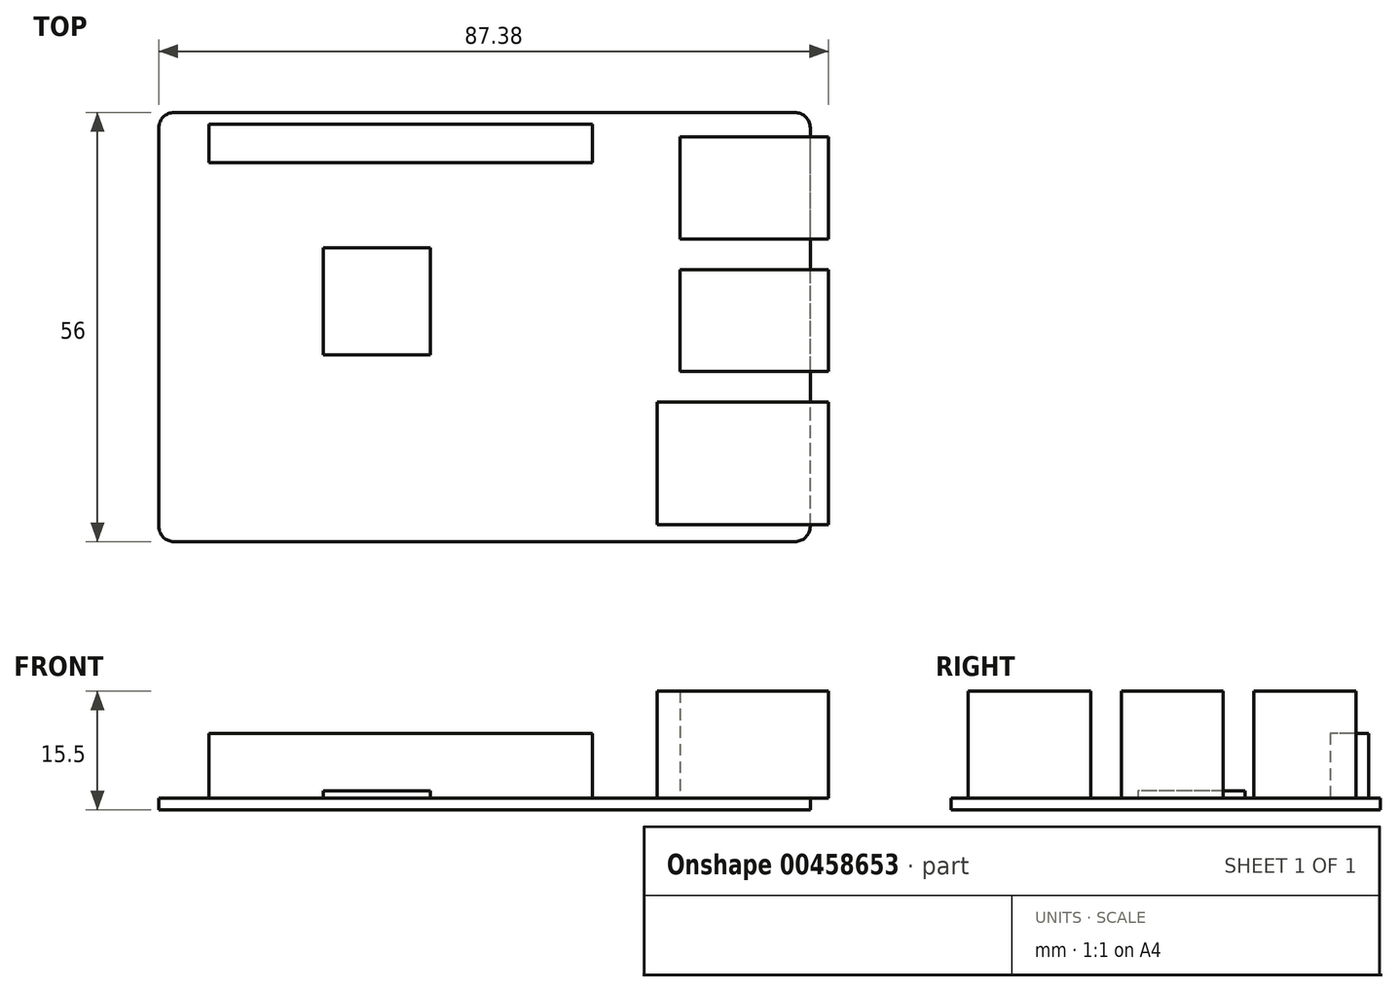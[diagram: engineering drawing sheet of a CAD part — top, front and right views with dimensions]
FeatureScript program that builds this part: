
annotation { "Feature Type Name" : "Feature", "Feature Type Description" : "" }
export const myFeature = defineFeature(function(context is Context, id is Id, definition is map)
    precondition{}
    {
        {
            var Q0;
            Q0=qCreatedBy(makeId("Top.planeOp"),FACE);
            var sketch = newSketch(context, id + "F0", { "sketchPlane" : qUnion([Q0])});
            skLineSegment(sketch, "E0.bottom", {"start": v(42.5, -28) * mm, "end": v(-42.5, -28) * mm});
            skLineSegment(sketch, "E0.top", {"start": v(42.5, 28) * mm, "end": v(-42.5, 28) * mm});
            skLineSegment(sketch, "E0.left", {"start": v(42.5, -28) * mm, "end": v(42.5, 28) * mm});
            skLineSegment(sketch, "E0.right", {"start": v(-42.5, -28) * mm, "end": v(-42.5, 28) * mm});
            skPoint(sketch, "E0.middle", {"position": v(0, 0) * mm});
            skSolve(sketch);
        }
        {
            var Q0;
            Q0=makeQuery(id+"F0.imprint","IMPRINT",FACE,{"disambiguationData":[TD([[makeQuery(id+"F0.imprint","IMPRINT",EDGE,{"derivedFrom":sQuery(id+"F0.wireOp",EDGE,"E0.bottom")}),-1.0]])]});
            extrude(context, id + "F1", {"entities" : qUnion([Q0]), "depth" : 1.5 * mm});
        }
        {
            var Q0;
            Q0=makeQuery(id+"F1.opExtrude","SWEPT_EDGE",EDGE,{"disambiguationData":[OSD([sQuery(id+"F0.wireOp",EDGE,"E0.bottom"),sQuery(id+"F0.wireOp",EDGE,"E0.right")])]});
            var Q1;
            Q1=makeQuery(id+"F1.opExtrude","SWEPT_EDGE",EDGE,{"disambiguationData":[OSD([sQuery(id+"F0.wireOp",EDGE,"E0.top"),sQuery(id+"F0.wireOp",EDGE,"E0.right")])]});
            var Q2;
            Q2=makeQuery(id+"F1.opExtrude","SWEPT_EDGE",EDGE,{"disambiguationData":[OSD([sQuery(id+"F0.wireOp",EDGE,"E0.bottom"),sQuery(id+"F0.wireOp",EDGE,"E0.left")])]});
            var Q3;
            Q3=makeQuery(id+"F1.opExtrude","SWEPT_EDGE",EDGE,{"disambiguationData":[OSD([sQuery(id+"F0.wireOp",EDGE,"E0.top"),sQuery(id+"F0.wireOp",EDGE,"E0.left")])]});
            fillet(context, id + "F2", {"entities" : qUnion([Q0, Q1, Q2, Q3]), "radius" : 2 * mm, "tangentPropagation" : true, "allowEdgeOverflow" : false});
        }
        {
            var Q0;
            Q0=makeQuery(id+"F1.opExtrude","CAP_FACE",FACE,{"disambiguationData":[OSD([sQuery(id+"F0.wireOp",EDGE,"E0.bottom"),sQuery(id+"F0.wireOp",EDGE,"E0.top"),sQuery(id+"F0.wireOp",EDGE,"E0.left"),sQuery(id+"F0.wireOp",EDGE,"E0.right")])],"isStart":false});
            var sketch = newSketch(context, id + "F3", { "sketchPlane" : qUnion([Q0])});
            skLineSegment(sketch, "E1.bottom", {"start": v(-35.96, 26.48) * mm, "end": v(14.04, 26.48) * mm});
            skLineSegment(sketch, "E1.top", {"start": v(-35.96, 21.48) * mm, "end": v(14.04, 21.48) * mm});
            skLineSegment(sketch, "E1.left", {"start": v(-35.96, 26.48) * mm, "end": v(-35.96, 21.48) * mm});
            skLineSegment(sketch, "E1.right", {"start": v(14.04, 26.48) * mm, "end": v(14.04, 21.48) * mm});
            skSolve(sketch);
        }
        {
            var Q0;
            Q0=makeQuery(id+"F3.imprint","IMPRINT",FACE,{"disambiguationData":[TD([[makeQuery(id+"F3.imprint","IMPRINT",EDGE,{"derivedFrom":sQuery(id+"F3.wireOp",EDGE,"E1.bottom")}),-1.0]])]});
            extrude(context, id + "F4", {"entities" : qUnion([Q0]), "operationType" : NewBodyOperationType.ADD, "depth" : 8.5 * mm});
        }
        {
            var Q0;
            Q0=makeQuery(id+"F1.opExtrude","CAP_FACE",FACE,{"disambiguationData":[OSD([sQuery(id+"F0.wireOp",EDGE,"E0.bottom"),sQuery(id+"F0.wireOp",EDGE,"E0.top"),sQuery(id+"F0.wireOp",EDGE,"E0.left"),sQuery(id+"F0.wireOp",EDGE,"E0.right")])],"isStart":false});
            var sketch = newSketch(context, id + "F5", { "sketchPlane" : qUnion([Q0])});
            skLineSegment(sketch, "E2.bottom", {"start": v(42.5, 24.8) * mm, "end": v(25.5, 24.8) * mm});
            skLineSegment(sketch, "E2.top", {"start": v(42.5, 11.5) * mm, "end": v(25.5, 11.5) * mm});
            skLineSegment(sketch, "E2.left", {"start": v(42.5, 24.8) * mm, "end": v(42.5, 11.5) * mm});
            skLineSegment(sketch, "E2.right", {"start": v(25.5, 24.8) * mm, "end": v(25.5, 11.5) * mm});
            skLineSegment(sketch, "E3.bottom", {"start": v(42.5, 7.5) * mm, "end": v(25.5, 7.5) * mm});
            skLineSegment(sketch, "E3.top", {"start": v(42.5, -5.8) * mm, "end": v(25.5, -5.8) * mm});
            skLineSegment(sketch, "E3.left", {"start": v(42.5, 7.5) * mm, "end": v(42.5, -5.8) * mm});
            skLineSegment(sketch, "E3.right", {"start": v(25.5, 7.5) * mm, "end": v(25.5, -5.8) * mm});
            skLineSegment(sketch, "E4.bottom", {"start": v(42.5, -9.8) * mm, "end": v(22.5, -9.8) * mm});
            skLineSegment(sketch, "E4.top", {"start": v(42.5, -25.8) * mm, "end": v(22.5, -25.8) * mm});
            skLineSegment(sketch, "E4.left", {"start": v(42.5, -9.8) * mm, "end": v(42.5, -25.8) * mm});
            skLineSegment(sketch, "E4.right", {"start": v(22.5, -9.8) * mm, "end": v(22.5, -25.8) * mm});
            skSolve(sketch);
        }
        {
            var Q0;
            Q0=makeQuery(id+"F5.imprint","IMPRINT",FACE,{"disambiguationData":[TD([[makeQuery(id+"F5.imprint","IMPRINT",EDGE,{"derivedFrom":sQuery(id+"F5.wireOp",EDGE,"E2.bottom")}),1.0]])]});
            var Q1;
            Q1=makeQuery(id+"F5.imprint","IMPRINT",FACE,{"disambiguationData":[TD([[makeQuery(id+"F5.imprint","IMPRINT",EDGE,{"derivedFrom":sQuery(id+"F5.wireOp",EDGE,"E3.bottom")}),1.0]])]});
            var Q2;
            {var subQ5=sQuery(id+"F5.wireOp",EDGE,"E4.bottom");Q2=makeQuery(id+"F5.imprint","IMPRINT",FACE,{"disambiguationData":[TD([[makeQuery(id+"F5.imprint","IMPRINT",EDGE,{"derivedFrom":subQ5}),1.0]])]});}
            extrude(context, id + "F6", {"entities" : qUnion([Q0, Q1, Q2]), "operationType" : NewBodyOperationType.ADD, "depth" : 14 * mm});
        }
        {
            var Q0;
            Q0=makeQuery(id+"F6.boolean.opBoolean","MERGE",FACE,{"derivedFrom":[makeQuery(id+"F1.opExtrude","SWEPT_FACE",FACE,{"disambiguationData":[OSD([sQuery(id+"F0.wireOp",EDGE,"E0.left")])]}),makeQuery(id+"F6.opExtrude","SWEPT_FACE",FACE,{"disambiguationData":[OSD([sQuery(id+"F5.wireOp",EDGE,"E2.left")])]}),makeQuery(id+"F6.opExtrude","SWEPT_FACE",FACE,{"disambiguationData":[OSD([sQuery(id+"F5.wireOp",EDGE,"E3.left")])]}),makeQuery(id+"F6.opExtrude","SWEPT_FACE",FACE,{"disambiguationData":[OSD([sQuery(id+"F5.wireOp",EDGE,"E4.left")])]})]});
            var sketch = newSketch(context, id + "F7", { "sketchPlane" : qUnion([Q0])});
            skLineSegment(sketch, "E5.bottom", {"start": v(-25.8, 15.5) * mm, "end": v(-9.8, 15.5) * mm});
            skLineSegment(sketch, "E5.top", {"start": v(-25.8, 1.5) * mm, "end": v(-9.8, 1.5) * mm});
            skLineSegment(sketch, "E5.left", {"start": v(-25.8, 15.5) * mm, "end": v(-25.8, 1.5) * mm});
            skLineSegment(sketch, "E5.right", {"start": v(-9.8, 15.5) * mm, "end": v(-9.8, 1.5) * mm});
            skLineSegment(sketch, "E6.bottom", {"start": v(-5.8, 15.5) * mm, "end": v(7.5, 15.5) * mm});
            skLineSegment(sketch, "E6.top", {"start": v(-5.8, 1.5) * mm, "end": v(7.5, 1.5) * mm});
            skLineSegment(sketch, "E6.left", {"start": v(-5.8, 15.5) * mm, "end": v(-5.8, 1.5) * mm});
            skLineSegment(sketch, "E6.right", {"start": v(7.5, 15.5) * mm, "end": v(7.5, 1.5) * mm});
            skLineSegment(sketch, "E7.bottom", {"start": v(11.5, 15.5) * mm, "end": v(24.8, 15.5) * mm});
            skLineSegment(sketch, "E7.top", {"start": v(11.5, 1.5) * mm, "end": v(24.8, 1.5) * mm});
            skLineSegment(sketch, "E7.left", {"start": v(11.5, 15.5) * mm, "end": v(11.5, 1.5) * mm});
            skLineSegment(sketch, "E7.right", {"start": v(24.8, 15.5) * mm, "end": v(24.8, 1.5) * mm});
            skSolve(sketch);
        }
        {
            var Q0;
            Q0=makeQuery(id+"F7.imprint","IMPRINT",FACE,{"disambiguationData":[TD([[makeQuery(id+"F7.imprint","IMPRINT",EDGE,{"derivedFrom":sQuery(id+"F7.wireOp",EDGE,"E5.bottom")}),-1.0]])]});
            var Q1;
            Q1=makeQuery(id+"F7.imprint","IMPRINT",FACE,{"disambiguationData":[TD([[makeQuery(id+"F7.imprint","IMPRINT",EDGE,{"derivedFrom":sQuery(id+"F7.wireOp",EDGE,"E6.bottom")}),-1.0]])]});
            var Q2;
            Q2=makeQuery(id+"F7.imprint","IMPRINT",FACE,{"disambiguationData":[TD([[makeQuery(id+"F7.imprint","IMPRINT",EDGE,{"derivedFrom":sQuery(id+"F7.wireOp",EDGE,"E7.bottom")}),-1.0]])]});
            extrude(context, id + "F8", {"entities" : qUnion([Q0, Q1, Q2]), "operationType" : NewBodyOperationType.ADD, "depth" : 2.38 * mm});
        }
        {
            var Q0;
            Q0=makeQuery(id+"F1.opExtrude","CAP_FACE",FACE,{"disambiguationData":[OSD([sQuery(id+"F0.wireOp",EDGE,"E0.bottom"),sQuery(id+"F0.wireOp",EDGE,"E0.top"),sQuery(id+"F0.wireOp",EDGE,"E0.left"),sQuery(id+"F0.wireOp",EDGE,"E0.right")])],"isStart":false});
            var sketch = newSketch(context, id + "F9", { "sketchPlane" : qUnion([Q0])});
            skLineSegment(sketch, "E8.bottom", {"start": v(-21.05, 10.37) * mm, "end": v(-7.05, 10.37) * mm});
            skLineSegment(sketch, "E8.top", {"start": v(-21.05, -3.63) * mm, "end": v(-7.05, -3.63) * mm});
            skLineSegment(sketch, "E8.left", {"start": v(-21.05, 10.37) * mm, "end": v(-21.05, -3.63) * mm});
            skLineSegment(sketch, "E8.right", {"start": v(-7.05, 10.37) * mm, "end": v(-7.05, -3.63) * mm});
            skSolve(sketch);
        }
        {
            var Q0;
            Q0=makeQuery(id+"F9.imprint","IMPRINT",FACE,{"disambiguationData":[TD([[makeQuery(id+"F9.imprint","IMPRINT",EDGE,{"derivedFrom":sQuery(id+"F9.wireOp",EDGE,"E8.bottom")}),-1.0]])]});
            extrude(context, id + "F10", {"entities" : qUnion([Q0]), "operationType" : NewBodyOperationType.ADD, "depth" : 1 * mm});
        }
    });
